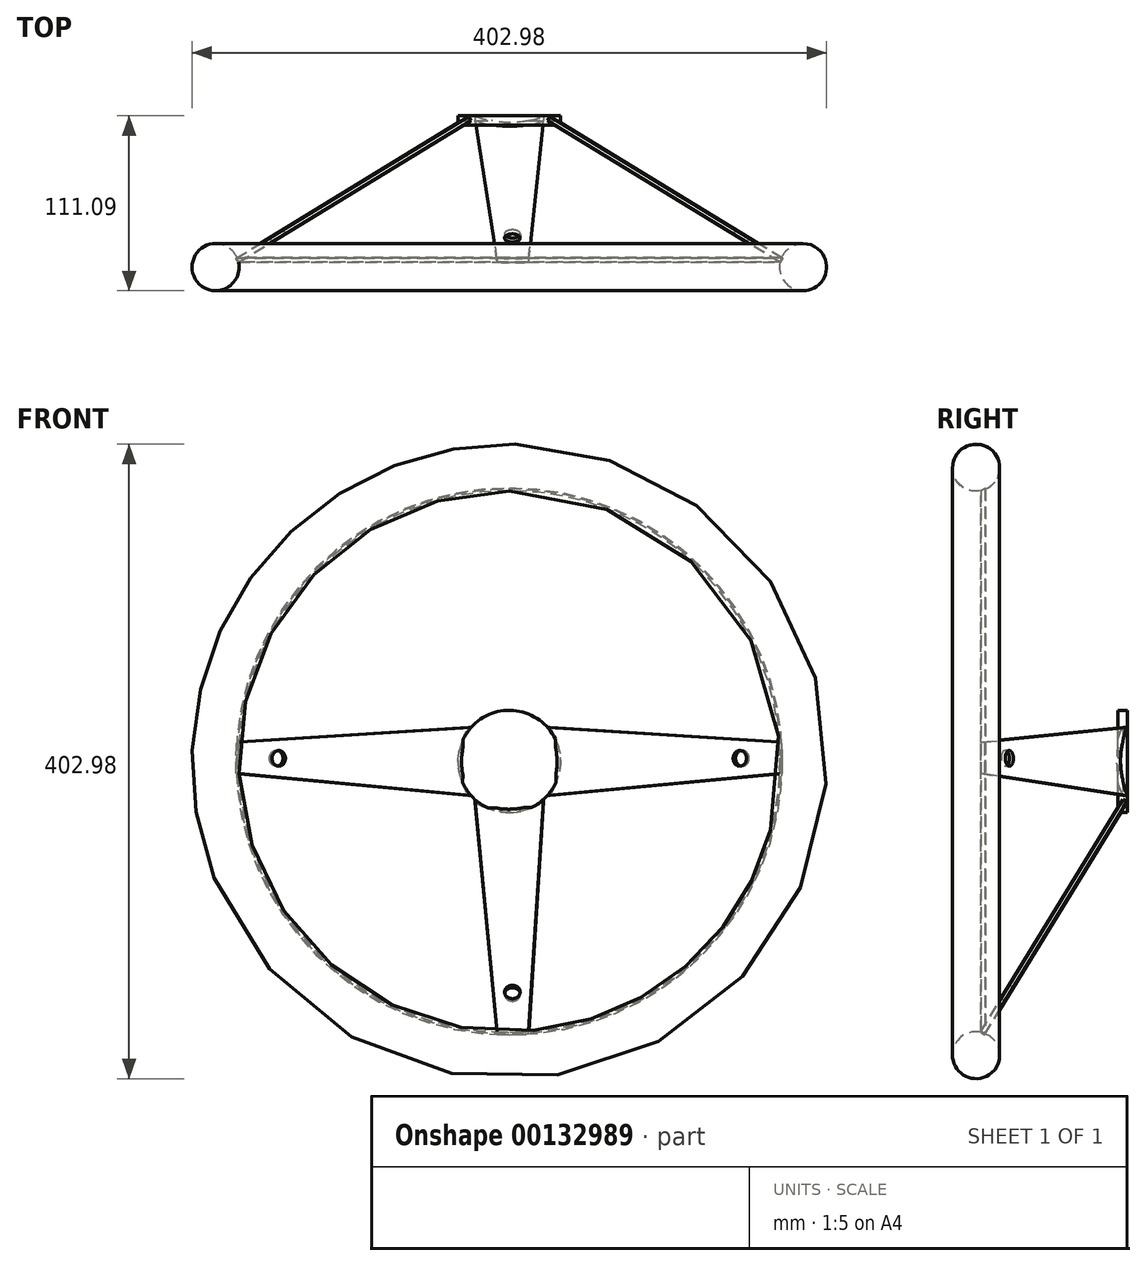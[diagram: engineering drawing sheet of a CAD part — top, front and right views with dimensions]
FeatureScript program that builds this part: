
annotation { "Feature Type Name" : "Feature", "Feature Type Description" : "" }
export const myFeature = defineFeature(function(context is Context, id is Id, definition is map)
    precondition{}
    {
        {
            var Q0;
            Q0=qCreatedBy(makeId("Front.planeOp"),FACE);
            cPlane(context, id + "F0", {"entities" : qUnion([Q0]), "cplaneType" : CPlaneType.OFFSET, "offset" : 90 * mm, "oppositeDirection" : true, "width" : 150 * mm, "height" : 150 * mm});
        }
        {
            var Q0;
            Q0=qCreatedBy(id+"F0.planeOp",FACE);
            var sketch = newSketch(context, id + "F1", { "sketchPlane" : qUnion([Q0])});
            skCircle(sketch, "E0", {"center": v(0, 0) * mm, "radius": 27.5 * mm});
            skCircle(sketch, "E1", {"center": v(0, 0) * mm, "radius": 32.5 * mm});
            skPoint(sketch, "E2", {"position": v(-24.22, 21.67) * mm});
            skPoint(sketch, "E3", {"position": v(-24.22, -21.67) * mm});
            skSolve(sketch);
        }
        {
            var Q0;
            Q0=qCreatedBy(makeId("Front.planeOp"),FACE);
            var sketch = newSketch(context, id + "F2", { "sketchPlane" : qUnion([Q0])});
            skCircle(sketch, "E4", {"center": v(0, 0) * mm, "radius": 172 * mm});
            skLineSegment(sketch, "E5", {"start": v(0, 0) * mm, "end": v(-171.98, 2.32) * mm, "construction": true});
            skPoint(sketch, "E6", {"position": v(-171.56, 12.32) * mm});
            skPoint(sketch, "E7", {"position": v(-171.83, -7.68) * mm});
            skSolve(sketch);
        }
        {
            var Q0;
            Q0=sQuery(id+"F2.wireOp",VERTEX,"E6");
            var Q1;
            Q1=sQuery(id+"F2.wireOp",VERTEX,"E7");
            var Q2;
            Q2=sQuery(id+"F1.wireOp",VERTEX,"E2");
            cPlane(context, id + "F3", {"entities" : qUnion([Q0, Q1, Q2]), "cplaneType" : CPlaneType.THREE_POINT, "offset" : 25 * mm, "width" : 150 * mm, "height" : 150 * mm});
        }
        {
            var Q0;
            Q0=qCreatedBy(id+"F3.planeOp",FACE);
            var sketch = newSketch(context, id + "F4", { "sketchPlane" : qUnion([Q0])});
            skLineSegment(sketch, "E8", {"start": v(146.32, 12.32) * mm, "end": v(-26.37, 20.92) * mm});
            skLineSegment(sketch, "E9", {"start": v(146.64, -7.68) * mm, "end": v(-26.18, -22.41) * mm});
            skEllipticalArc(sketch, "E10.0", {});
            skEllipticalArc(sketch, "E11.0", {});
            const initialGuessF4  = {"E10.0": [-0.04694286756101271, -0.0007445066791525363, 0.01585785233934832, -0.9998742563538594, 0.0325, 0.027727626661568836, 0.8275385453073428, 2.2869938577612756], "E11.0": [0, 0, 0.01585785233934832, -0.9998742563538594, 0.172, 0.14674313187045662, 1.5126186569987574, 1.6289739965910373]};
            skSetInitialGuess(sketch, initialGuessF4);
            skSolve(sketch);
        }
        {
            var Q0;
            Q0 = qSketchRegion(id + "F4", true);
            extrude(context, id + "F5", {"entities" : qUnion([Q0]), "depth" : 3 * mm});
        }
        {
            var Q0;
            Q0=qCreatedBy(makeId("Front.planeOp"),FACE);
            var sketch = newSketch(context, id + "F6", { "sketchPlane" : qUnion([Q0])});
            skPoint(sketch, "E12", {"position": v(-136.99, 1.85) * mm});
            skSolve(sketch);
        }
        {
            var Q0;
            Q0=makeQuery(id+"F5.opExtrude","CAP_FACE",FACE,{"disambiguationData":[OSD([sQuery(id+"F4.wireOp",EDGE,"E8"),sQuery(id+"F4.wireOp",EDGE,"E9"),sQuery(id+"F4.wireOp",EDGE,"E10.0"),sQuery(id+"F4.wireOp",EDGE,"E11.0")])],"isStart":true});
            var sketch = newSketch(context, id + "F7", { "sketchPlane" : qUnion([Q0])});
            skLineSegment(sketch, "E13.0", {"start": v(0, 0) * mm, "end": v(-146.72, 2.32) * mm});
            skPoint(sketch, "E14.0", {"position": v(-116.87, 1.85) * mm});
            skSolve(sketch);
        }
        {
            var Q0;
            Q0=sQuery(id+"F7.wireOp",VERTEX,"E14.0");
            var Q1;
            Q1=makeQuery(id+"F5.opExtrude","SWEPT_BODY",BODY,{"disambiguationData":[OSD([sQuery(id+"F4.wireOp",EDGE,"E8"),sQuery(id+"F4.wireOp",EDGE,"E9"),sQuery(id+"F4.wireOp",EDGE,"E10.0"),sQuery(id+"F4.wireOp",EDGE,"E11.0")])]});
            hole(context, id + "F8", {"style" : HoleStyle.SIMPLE, "endStyle" : HoleEndStyle.THROUGH, "holeDiameter" : 10 * mm, "locations" : qUnion([Q0]), "scope" : qUnion([Q1]), "isTappedThrough" : true});
        }
        {
            var Q0;
            Q0=makeQuery(id+"F5.opExtrude","SWEPT_BODY",BODY,{"disambiguationData":[OSD([sQuery(id+"F4.wireOp",EDGE,"E8"),sQuery(id+"F4.wireOp",EDGE,"E9"),sQuery(id+"F4.wireOp",EDGE,"E10.0"),sQuery(id+"F4.wireOp",EDGE,"E11.0")])]});
            var Q1;
            Q1=qCreatedBy(makeId("Right.planeOp"),FACE);
            mirror(context, id + "F9", {"entities" : qUnion([Q0]), "mirrorPlane" : qUnion([Q1])});
        }
        {
            var Q0;
            Q0=makeQuery(id+"F9.opPattern","COPY",BODY,{"derivedFrom":makeQuery(id+"F5.opExtrude","SWEPT_BODY",BODY,{"disambiguationData":[OSD([sQuery(id+"F4.wireOp",EDGE,"E8"),sQuery(id+"F4.wireOp",EDGE,"E9"),sQuery(id+"F4.wireOp",EDGE,"E10.0"),sQuery(id+"F4.wireOp",EDGE,"E11.0")])]}),"instanceName":"1"});
            var Q1;
            Q1=sQuery(id+"F1.wireOp",EDGE,"E0");
            circularPattern(context, id + "F10", {"entities" : qUnion([Q0]), "axis" : qUnion([Q1]), "angle" : 90 * degree, "instanceCount" : 2, "oppositeDirection" : true});
        }
        {
            var Q0;
            Q0=makeQuery(id+"F1.imprint","IMPRINT",FACE,{"disambiguationData":[TD([[makeQuery(id+"F1.imprint","IMPRINT",EDGE,{"derivedFrom":sQuery(id+"F1.wireOp",EDGE,"E0")}),1.0]])]});
            var Q1;
            Q1=makeQuery(id+"F1.imprint","IMPRINT",FACE,{"disambiguationData":[TD([[makeQuery(id+"F1.imprint","IMPRINT",EDGE,{"derivedFrom":sQuery(id+"F1.wireOp",EDGE,"E0")}),-1.0]])]});
            var Q2;
            Q2 = qSketchRegion(id + "F6", true);
            extrude(context, id + "F11", {"entities" : qUnion([Q0, Q1, Q2]), "operationType" : NewBodyOperationType.ADD, "depth" : 3 * mm, "hasSecondDirection" : true, "secondDirectionOppositeDirection" : true, "secondDirectionDepth" : 3 * mm});
        }
        {
            var Q0;
            Q0=makeQuery(id+"F5.opExtrude","SWEPT_FACE",FACE,{"disambiguationData":[OSD([sQuery(id+"F4.wireOp",EDGE,"E9")])]});
            var sketch = newSketch(context, id + "F12", { "sketchPlane" : qUnion([Q0])});
            skCircle(sketch, "E15", {"center": v(-185.49, 2.87) * mm, "radius": 15 * mm});
            skSolve(sketch);
        }
        {
            var Q0;
            {var subQ1=sQuery(id+"F4.wireOp",EDGE,"E9");var subQ2=makeQuery(id+"F5.opExtrude","SWEPT_EDGE",EDGE,{"disambiguationData":[OSD([subQ1,sQuery(id+"F4.wireOp",EDGE,"E11.0")])]});Q0=makeQuery(id+"F12.imprint","IMPRINT",FACE,{"disambiguationData":[TD([[makeQuery(id+"F12.imprint","IMPRINT",EDGE,{"derivedFrom":subQ2}),1.0]])]});}
            var Q1;
            Q1=sQuery(id+"F12.wireOp",EDGE,"E15");
            var Q2;
            Q2=sQuery(id+"F2.wireOp",EDGE,"E4");
            revolve(context, id + "F13", {"entities" : qUnion([Q0]), "surfaceEntities" : qUnion([Q1]), "axis" : qUnion([Q2]), "revolveType" : RevolveType.FULL});
        }
    });
